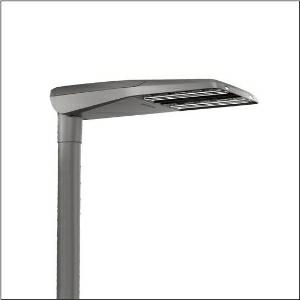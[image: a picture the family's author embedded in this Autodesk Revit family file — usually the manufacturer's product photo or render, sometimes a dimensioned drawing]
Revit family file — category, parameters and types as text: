
# Revit family: streetlight_sl_11_iq_midi___st1_2a_5xc3a41e08me_8609
name_source: partatom
category: Lighting Fixtures
units: mm (PartAtom-declared; Revit-internal decimal feet)

## family parameters
Cut with Voids When Loaded = No
Host = Face
Light Source = No
Part Type = Normal
Room Calculation Point = No
Round Connector Dimension = Use Diameter
Shared = No

## types (1)
- --- (1 x LED, 18900 lm, 124.7 W, 4000K)
    Apparent Load = 125 VA
    CIE Flux Codes = 32 70 96 100 100
    Color Rendering = 70
    Color Temperature = 4000K
    Default Elevation = 1800 mm
    Description = Streetlight SL 11 iQ midi, mast luminaire, primary light control with 3 zone facetted reflector, of plastic, silver coated, highly specular, primary optical cover: cover, of PMMA, transparent, light distribution: ST1.2a, light emission: direct distribution, primary light characteristic: asymmetric, installation type: post-top, side-entry, lamps: LED, High Power LED, rated values: 18.900lm | 124,7W | 151,6lm/W (begin service life); end service life: 18.900lm | 132,2W; at 50% lumin. flux: 9.450lm | 57,4W | 164,6lm/W, colour temperature: 4000K, colour rendering: CRI > 70, light colour: 740, light setting 1 begin service life: 100% | 18.900lm | 124,7W | 151,6lm/W | 4.000K, light setting 1 end service life: 132,2W, further light settings possible, control: optimised constant luminous flux control (CLO 2.0), Desk-Remote (wireless, voltage-free reading and setting of iQ features in the workshop via application-optimized NFC function/RFID function), Light-Fading, Smart-Wire, Night-Set, Lumen-Switch, Temp-Guard, Auto-Match, with cable H07RN-F 5x 1.5mm², mains connection: 230..240V, AC, 50/60Hz, connection cable pre-assembled, cable length: 12,5m, luminaire housing, of diecast aluminium, powder-coated, Siteco® metallic grey (DB 702S), please order mast flange separately, inclination adjustable without tools: 0°, 5°, 10°, 15° (post-top) | 0°, -5°, -10°, -15° (side-entry), sealing non-destructively replaceable, multi-level sealing system, length: 780mm, width: 376mm, height: 118mm, mast flange for spigot size: 42mm (side-entry): 5XC10008XM4, 60/48mm (side-entry/post-top): 5XC10108XM2, 76/60mm (side-entry/post-top): 5XC10108XM1, equipment: Power, protection rating (complete): IP66, insulation class (complete): insulation class II (safety insulation), certification: CE, ENEC, ENEC+, VDE, impact resistance: IK10, permissible operating ambient temperature for outdoor applications: -25..+50°C, standard-compliant lighting for roads and squares, Environmental Product Declaration (EPD) tested and certified by an independent institute, packaging unit: 1 piece

Light Distribution: ST1.2a
    Height = 118 mm
    Lamp = 1 x LED
    Lamp Light Flux = 18900 lm
    Lamp Power = 124.7 W
    Lamp count = 1
    Length = 780 mm
    Luminous efficacy = 152 lm/W
    Manufacturer = Siteco
    ModVariant = No
    Model = 5XC3A41E08ME
    Number of Poles = 1
    OnlyDefault = Yes
    Power Factor = 1
    Product Name = Streetlight SL 11 iQ midi | ST1.2a
    Product group = mast luminaire | pylon top
    ProductGroupID = 6100
    Protection Class = Protection class II
    Protection Degree = IP 66
    RLX_Detail_Level = 1
    RLX_Emergency_Light_Flux = 0 lm
    RLX_Emergency_Type = 0
    RLX_Emergency_Type_DB = No
    RlxData = <blob elided: 71013 chars, md5=b4d81026>
    Socket = socket
    Standby Power = 0 W
    System Light Flux = 18900 lm
    System Power = 125 W
    Type Comments = factory setting: luminous flux: 100 % | dim-lin: 254 | 557 mA
    Type Image = l_1005960.jpg
    URL = http://relux.com
    VarID = @adj_196334
    Voltage = 0 V
    Weight = 0.00 kg
    Width = 376 mm

## geometry (parser evidence)
native form markers: Blend x4, Sweep x10
no freeform markers — native parametric forms only
